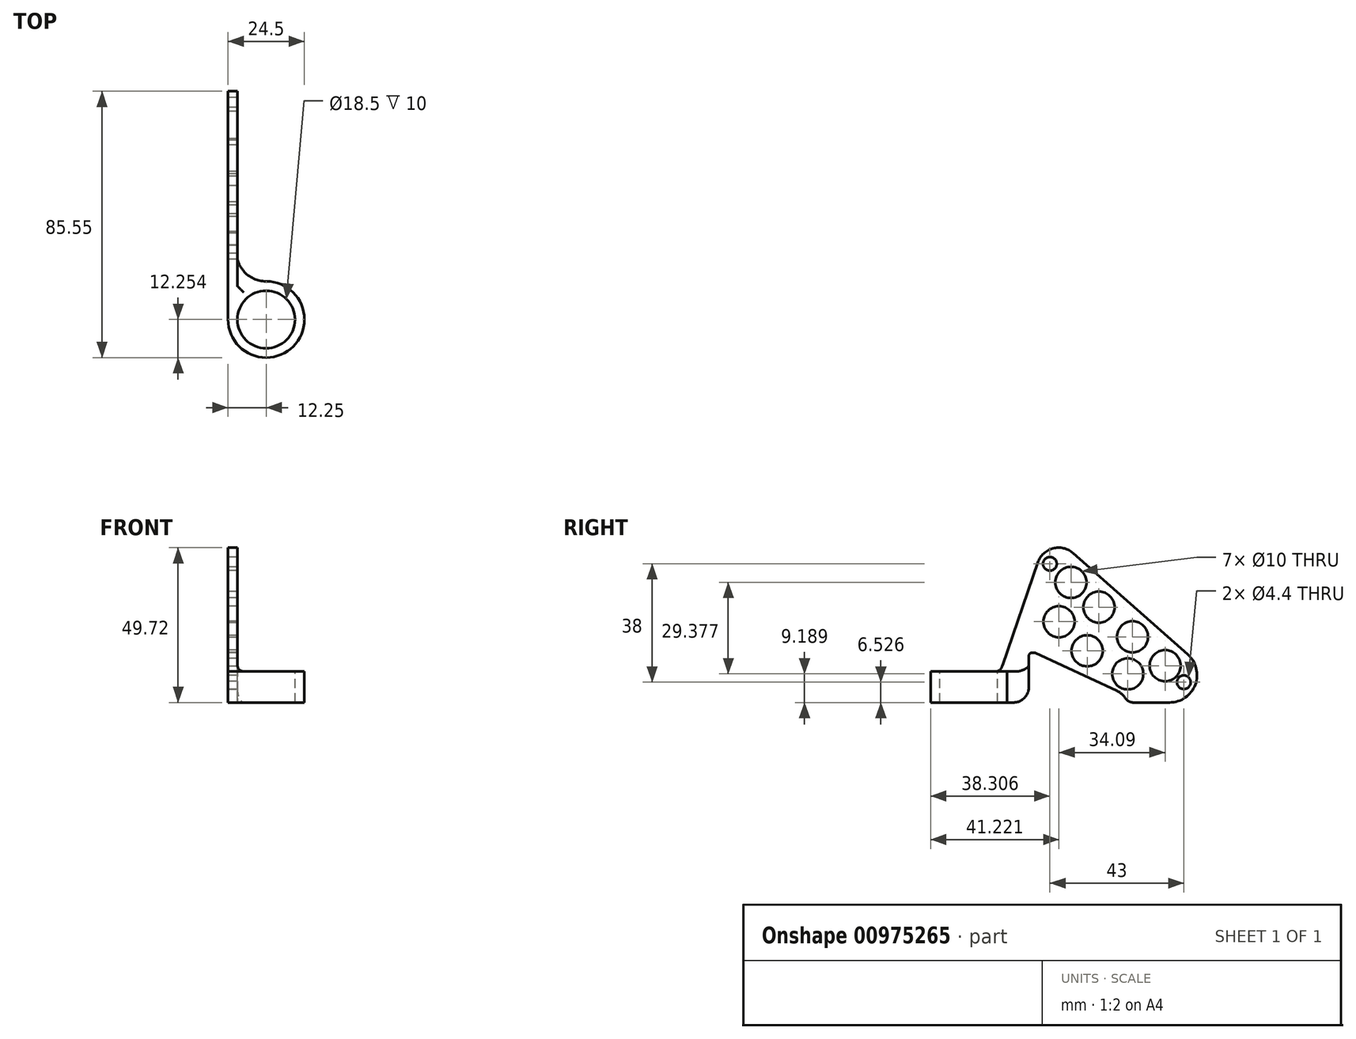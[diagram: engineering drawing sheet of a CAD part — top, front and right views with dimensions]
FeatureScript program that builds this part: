
annotation { "Feature Type Name" : "Feature", "Feature Type Description" : "" }
export const myFeature = defineFeature(function(context is Context, id is Id, definition is map)
    precondition{}
    {
        {
            assignVariable(context, id + "F0", {"name" : "zProbeHolderHeight", "anyValue" : 10});
        }
        {
            var Q0;
            Q0=qCreatedBy(makeId("Right.planeOp"),FACE);
            var sketch = newSketch(context, id + "F1", { "sketchPlane" : qUnion([Q0])});
            skArc(sketch, "E0", {"start": v(42.92, 23.14) * mm, "mid": v(37.92, 39.24) * mm, "end": v(21.32, 42.23) * mm});
            skPoint(sketch, "E1", {"position": v(5.66, 46.07) * mm});
            skPoint(sketch, "E2", {"position": v(48.66, 8.07) * mm});
            skCircle(sketch, "E3", {"center": v(5.66, 46.07) * mm, "radius": 2.2 * mm});
            skCircle(sketch, "E4", {"center": v(48.66, 8.07) * mm, "radius": 2.2 * mm});
            skArc(sketch, "E5", {"start": v(50.56, 16.33) * mm, "mid": v(44.23, 46.35) * mm, "end": v(13.66, 49) * mm});
            skArc(sketch, "E6", {"start": v(51.43, 5.62) * mm, "mid": v(51.72, 6) * mm, "end": v(51.96, 6.4) * mm});
            skArc(sketch, "E7", {"start": v(2.88, 48.52) * mm, "mid": v(2.72, 48.31) * mm, "end": v(2.57, 48.1) * mm});
            skLineSegment(sketch, "E8", {"start": v(53.64, 3.66) * mm, "end": v(0, 51.06) * mm, "construction": true});
            skLineSegment(sketch, "E9", {"start": v(0.92, 17.54) * mm, "end": v(-0.08, 17.54) * mm});
            skLineSegment(sketch, "E10", {"start": v(0.92, 17.54) * mm, "end": v(27.16, 5.32) * mm});
            skArc(sketch, "E11", {"start": v(29.9, 2.92) * mm, "mid": v(28.7, 4.31) * mm, "end": v(27.16, 5.32) * mm});
            skPoint(sketch, "E12.end.orphan", {"position": v(27.16, 1.32) * mm});
            skPoint(sketch, "E12.start.orphan", {"position": v(1.4, 1.54) * mm});
            skLineSegment(sketch, "E13", {"start": v(32.42, 1.54) * mm, "end": v(44.09, 1.54) * mm});
            skLineSegment(sketch, "E14", {"start": v(13.1, 49.5) * mm, "end": v(49.92, 16.96) * mm});
            skArc(sketch, "E15.filletArc", {"start": v(13.1, 49.5) * mm, "mid": v(6.65, 51.03) * mm, "end": v(1.79, 46.52) * mm});
            skArc(sketch, "E16.filletArc", {"start": v(44.09, 1.54) * mm, "mid": v(52.33, 7.24) * mm, "end": v(49.92, 16.96) * mm});
            skLineSegment(sketch, "E17", {"start": v(-1.08, 16.54) * mm, "end": v(-1.08, 16.54) * mm});
            skLineSegment(sketch, "E18", {"start": v(-6.08, 1.54) * mm, "end": v(-12.36, 1.54) * mm});
            skLineSegment(sketch, "E19", {"start": v(-12.36, 1.54) * mm, "end": v(-12.36, 11.54) * mm});
            skPoint(sketch, "E20.visualSharp", {"position": v(-1.08, 1.54) * mm});
            skPoint(sketch, "E21.visualSharp", {"position": v(-1.08, 17.54) * mm});
            skArc(sketch, "E21.filletArc", {"start": v(-0.08, 17.54) * mm, "mid": v(-0.79, 17.25) * mm, "end": v(-1.08, 16.54) * mm});
            skCircle(sketch, "E22", {"center": v(12.4, 40.1) * mm, "radius": 5 * mm});
            skCircle(sketch, "E23", {"center": v(21.4, 32.15) * mm, "radius": 5 * mm});
            skCircle(sketch, "E24", {"center": v(32.17, 22.63) * mm, "radius": 5 * mm});
            skCircle(sketch, "E25", {"center": v(42.66, 13.36) * mm, "radius": 5 * mm});
            skCircle(sketch, "E26", {"center": v(30.66, 10.73) * mm, "radius": 5 * mm});
            skCircle(sketch, "E27", {"center": v(17.62, 18.14) * mm, "radius": 5 * mm});
            skCircle(sketch, "E28", {"center": v(8.57, 27.48) * mm, "radius": 5 * mm});
            skLineSegment(sketch, "E29", {"start": v(-1.08, 6.54) * mm, "end": v(-1.08, 16.54) * mm});
            skPoint(sketch, "E30.visualSharp", {"position": v(-7.09, 11.54) * mm});
            skArc(sketch, "E31.filletArc", {"start": v(-6.08, 1.54) * mm, "mid": v(-2.55, 3) * mm, "end": v(-1.08, 6.54) * mm});
            skLineSegment(sketch, "E32", {"start": v(-12.36, 11.54) * mm, "end": v(-10.27, 11.54) * mm});
            skLineSegment(sketch, "E33", {"start": v(-10.27, 11.54) * mm, "end": v(1.79, 46.52) * mm});
            skPoint(sketch, "E34.visualSharp", {"position": v(-10.27, 11.54) * mm});
            skPoint(sketch, "E35.visualSharp", {"position": v(30.57, 1.54) * mm});
            skArc(sketch, "E35.filletArc", {"start": v(29.9, 2.92) * mm, "mid": v(30.98, 1.91) * mm, "end": v(32.42, 1.54) * mm});
            skSolve(sketch);
        }
        {
            var Q0;
            Q0=makeQuery(id+"F1.imprint","IMPRINT",FACE,{"disambiguationData":[TD([[makeQuery(id+"F1.imprint","IMPRINT",EDGE,{"derivedFrom":sQuery(id+"F1.wireOp",EDGE,"E3")}),-1.0]])]});
            extrude(context, id + "F2", {"entities" : qUnion([Q0]), "depth" : 3 * mm, "offsetDistance" : 25 * mm});
        }
        {
            var Q0;
            Q0=makeQuery(id+"F2.opExtrude","SWEPT_FACE",FACE,{"disambiguationData":[OSD([sQuery(id+"F1.wireOp",EDGE,"E32")])]});
            var sketch = newSketch(context, id + "F3", { "sketchPlane" : qUnion([Q0])});
            skCircle(sketch, "E36", {"center": v(12.25, -20.4) * mm, "radius": 9.25 * mm});
            skCircle(sketch, "E37", {"center": v(12.25, -20.4) * mm, "radius": 12.25 * mm});
            skPoint(sketch, "E38", {"position": v(3, -12.36) * mm});
            skPoint(sketch, "E39", {"position": v(0, -20.4) * mm});
            skLineSegment(sketch, "E40", {"start": v(12.25, -8.15) * mm, "end": v(0, -8.15) * mm});
            skLineSegment(sketch, "E41", {"start": v(0, -8.15) * mm, "end": v(0, -20.4) * mm});
            skSolve(sketch);
        }
        {
            var Q0;
            {var subQ0=sQuery(id+"F3.wireOp",EDGE,"UUcVxnHS-C4FE-dPSX-iT2G-Nc1NCUdjFzvL");Q0=makeQuery(id+"F3.imprint","IMPRINT",FACE,{"disambiguationData":[TD([[makeQuery(id+"F3.imprint","IMPRINT",EDGE,{"derivedFrom":subQ0}),1.0]])]});}
            var Q1;
            {var subQ0=sQuery(id+"F3.wireOp",EDGE,"E37");var subQ1=sQuery(id+"F1.wireOp",EDGE,"70Iaj5Xo-3E1D-0QHm-Mte3-s1jAJqJXMEIu");var subQ8=makeQuery(id+"F3.imprint","INTERSECT",VERTEX,{"derivedFrom":[makeQuery(id+"F2.opExtrude","CAP_EDGE",EDGE,{"disambiguationData":[OSD([subQ1])],"isStart":true}),subQ0]});Q1=makeQuery(id+"F3.imprint","IMPRINT",FACE,{"disambiguationData":[TD([[makeQuery(id+"F3.imprint","IMPRINT",EDGE,{"disambiguationData":[TD([[subQ8,1.0]])],"derivedFrom":subQ0}),1.0]])]});}
            var Q2;
            {var subQ0=sQuery(id+"F3.wireOp",EDGE,"E37");var subQ1=makeQuery(id+"F3.imprint","INTERSECT",VERTEX,{"derivedFrom":[subQ0,sQuery(id+"F3.wireOp",EDGE,"mMwxjC30-bNG6-h4qv-BiwM-IJgF43j1XXvy")]});Q2=makeQuery(id+"F3.imprint","IMPRINT",FACE,{"disambiguationData":[TD([[makeQuery(id+"F3.imprint","IMPRINT",EDGE,{"disambiguationData":[TD([[subQ1,-1.0]])],"derivedFrom":subQ0}),1.0]])]});}
            var Q3;
            {var subQ0=sQuery(id+"F3.wireOp",EDGE,"mMwxjC30-bNG6-h4qv-BiwM-IJgF43j1XXvy");var subQ1=sQuery(id+"F3.wireOp",EDGE,"E37");var subQ2=makeQuery(id+"F3.imprint","INTERSECT",VERTEX,{"derivedFrom":[subQ1,subQ0]});Q3=makeQuery(id+"F3.imprint","IMPRINT",FACE,{"disambiguationData":[TD([[makeQuery(id+"F3.imprint","IMPRINT",EDGE,{"disambiguationData":[TD([[subQ2,-1.0]])],"derivedFrom":subQ1}),-1.0]])]});}
            var Q4;
            {var subQ1=sQuery(id+"F1.wireOp",EDGE,"E32");var subQ2=makeQuery(id+"F2.opExtrude","SWEPT_EDGE",EDGE,{"disambiguationData":[OSD([sQuery(id+"F1.wireOp",EDGE,"E19"),subQ1])]});Q4=makeQuery(id+"F3.imprint","IMPRINT",FACE,{"disambiguationData":[TD([[makeQuery(id+"F3.imprint","IMPRINT",EDGE,{"derivedFrom":subQ2}),1.0]])]});}
            extrude(context, id + "F4", {"entities" : qUnion([Q0, Q1, Q2, Q3, Q4]), "operationType" : NewBodyOperationType.ADD, "oppositeDirection" : true, "depth" : (getVariable(context, 'zProbeHolderHeight')) * mm, "offsetDistance" : 25 * mm});
        }
        {
            var Q0;
            {var subQ0=sQuery(id+"F3.wireOp",EDGE,"NZoEJAki-vv1U-87aH-g5Ov-YUSqsTYzDlse");Q0=makeQuery(id+"F3.imprint","IMPRINT",FACE,{"disambiguationData":[TD([[makeQuery(id+"F3.imprint","IMPRINT",EDGE,{"derivedFrom":subQ0}),-1.0]])]});}
            var Q1;
            {var subQ0=sQuery(id+"F3.wireOp",EDGE,"E36");var subQ1=sQuery(id+"F1.wireOp",EDGE,"70Iaj5Xo-3E1D-0QHm-Mte3-s1jAJqJXMEIu");var subQ4=makeQuery(id+"F2.opExtrude","CAP_EDGE",EDGE,{"disambiguationData":[OSD([subQ1])],"isStart":false});var subQ5=makeQuery(id+"F3.imprint","INTERSECT",VERTEX,{"derivedFrom":[subQ4,subQ0]});Q1=makeQuery(id+"F3.imprint","IMPRINT",FACE,{"disambiguationData":[TD([[makeQuery(id+"F3.imprint","IMPRINT",EDGE,{"disambiguationData":[TD([[subQ5,-1.0]])],"derivedFrom":subQ0}),1.0]])]});}
            extrude(context, id + "F5", {"entities" : qUnion([Q0, Q1]), "operationType" : NewBodyOperationType.REMOVE, "oppositeDirection" : true, "depth" : 25 * mm, "offsetDistance" : 25 * mm});
        }
        {
            var Q0;
            Q0=makeQuery(id+"F4.boolean.opBoolean","INTERSECT",EDGE,{"derivedFrom":[makeQuery(id+"F2.opExtrude","CAP_FACE",FACE,{"disambiguationData":[OSD([sQuery(id+"F1.wireOp",EDGE,"E3"),sQuery(id+"F1.wireOp",EDGE,"E4"),sQuery(id+"F1.wireOp",EDGE,"E9"),sQuery(id+"F1.wireOp",EDGE,"E10"),sQuery(id+"F1.wireOp",EDGE,"E11"),sQuery(id+"F1.wireOp",EDGE,"E13"),sQuery(id+"F1.wireOp",EDGE,"E14"),sQuery(id+"F1.wireOp",EDGE,"E15.filletArc"),sQuery(id+"F1.wireOp",EDGE,"E16.filletArc"),sQuery(id+"F1.wireOp",EDGE,"E18"),sQuery(id+"F1.wireOp",EDGE,"E19"),sQuery(id+"F1.wireOp",EDGE,"E21.filletArc"),sQuery(id+"F1.wireOp",EDGE,"E22"),sQuery(id+"F1.wireOp",EDGE,"E23"),sQuery(id+"F1.wireOp",EDGE,"E24"),sQuery(id+"F1.wireOp",EDGE,"E25"),sQuery(id+"F1.wireOp",EDGE,"E26"),sQuery(id+"F1.wireOp",EDGE,"E27"),sQuery(id+"F1.wireOp",EDGE,"E28"),sQuery(id+"F1.wireOp",EDGE,"E29"),sQuery(id+"F1.wireOp",EDGE,"E31.filletArc"),sQuery(id+"F1.wireOp",EDGE,"E32"),sQuery(id+"F1.wireOp",EDGE,"E33"),sQuery(id+"F1.wireOp",EDGE,"E35.filletArc")])],"isStart":false}),makeQuery(id+"F4.opExtrude","SWEPT_FACE",FACE,{"disambiguationData":[OSD([sQuery(id+"F3.wireOp",EDGE,"E40")])]})]});
            fillet(context, id + "F6", {"entities" : qUnion([Q0]), "radius" : 9.5 * mm, "tangentPropagation" : true, "allowEdgeOverflow" : false});
        }
        {
            var Q0;
            {var subQ0=sQuery(id+"F1.wireOp",EDGE,"E33");var subQ1=sQuery(id+"F1.wireOp",EDGE,"E32");var subQ2=sQuery(id+"F1.wireOp",EDGE,"E19");Q0=makeQuery(id+"F4.boolean.opBoolean","INTERSECT",EDGE,{"derivedFrom":[makeQuery(id+"F2.opExtrude","CAP_FACE",FACE,{"disambiguationData":[OSD([sQuery(id+"F1.wireOp",EDGE,"E3"),sQuery(id+"F1.wireOp",EDGE,"E4"),sQuery(id+"F1.wireOp",EDGE,"E9"),sQuery(id+"F1.wireOp",EDGE,"E10"),sQuery(id+"F1.wireOp",EDGE,"E11"),sQuery(id+"F1.wireOp",EDGE,"E13"),sQuery(id+"F1.wireOp",EDGE,"E14"),sQuery(id+"F1.wireOp",EDGE,"E15.filletArc"),sQuery(id+"F1.wireOp",EDGE,"E16.filletArc"),sQuery(id+"F1.wireOp",EDGE,"E18"),subQ2,sQuery(id+"F1.wireOp",EDGE,"E21.filletArc"),sQuery(id+"F1.wireOp",EDGE,"E22"),sQuery(id+"F1.wireOp",EDGE,"E23"),sQuery(id+"F1.wireOp",EDGE,"E24"),sQuery(id+"F1.wireOp",EDGE,"E25"),sQuery(id+"F1.wireOp",EDGE,"E26"),sQuery(id+"F1.wireOp",EDGE,"E27"),sQuery(id+"F1.wireOp",EDGE,"E28"),sQuery(id+"F1.wireOp",EDGE,"E29"),sQuery(id+"F1.wireOp",EDGE,"E31.filletArc"),subQ1,subQ0,sQuery(id+"F1.wireOp",EDGE,"E35.filletArc")])],"isStart":false}),makeQuery(id+"F4.opExtrude","CAP_FACE",FACE,{"disambiguationData":[OSD([subQ2,subQ1,subQ0,sQuery(id+"F3.wireOp",EDGE,"E36"),sQuery(id+"F3.wireOp",EDGE,"E37"),sQuery(id+"F3.wireOp",EDGE,"E40"),sQuery(id+"F3.wireOp",EDGE,"E41")])],"isStart":true})]});}
            var Q1;
            Q1=makeQuery(id+"F2.opExtrude","SWEPT_EDGE",EDGE,{"disambiguationData":[OSD([sQuery(id+"F1.wireOp",EDGE,"E32"),sQuery(id+"F1.wireOp",EDGE,"E33")])]});
            fillet(context, id + "F7", {"entities" : qUnion([Q0, Q1]), "radius" : 2 * mm, "tangentPropagation" : true, "allowEdgeOverflow" : false});
        }
    });
